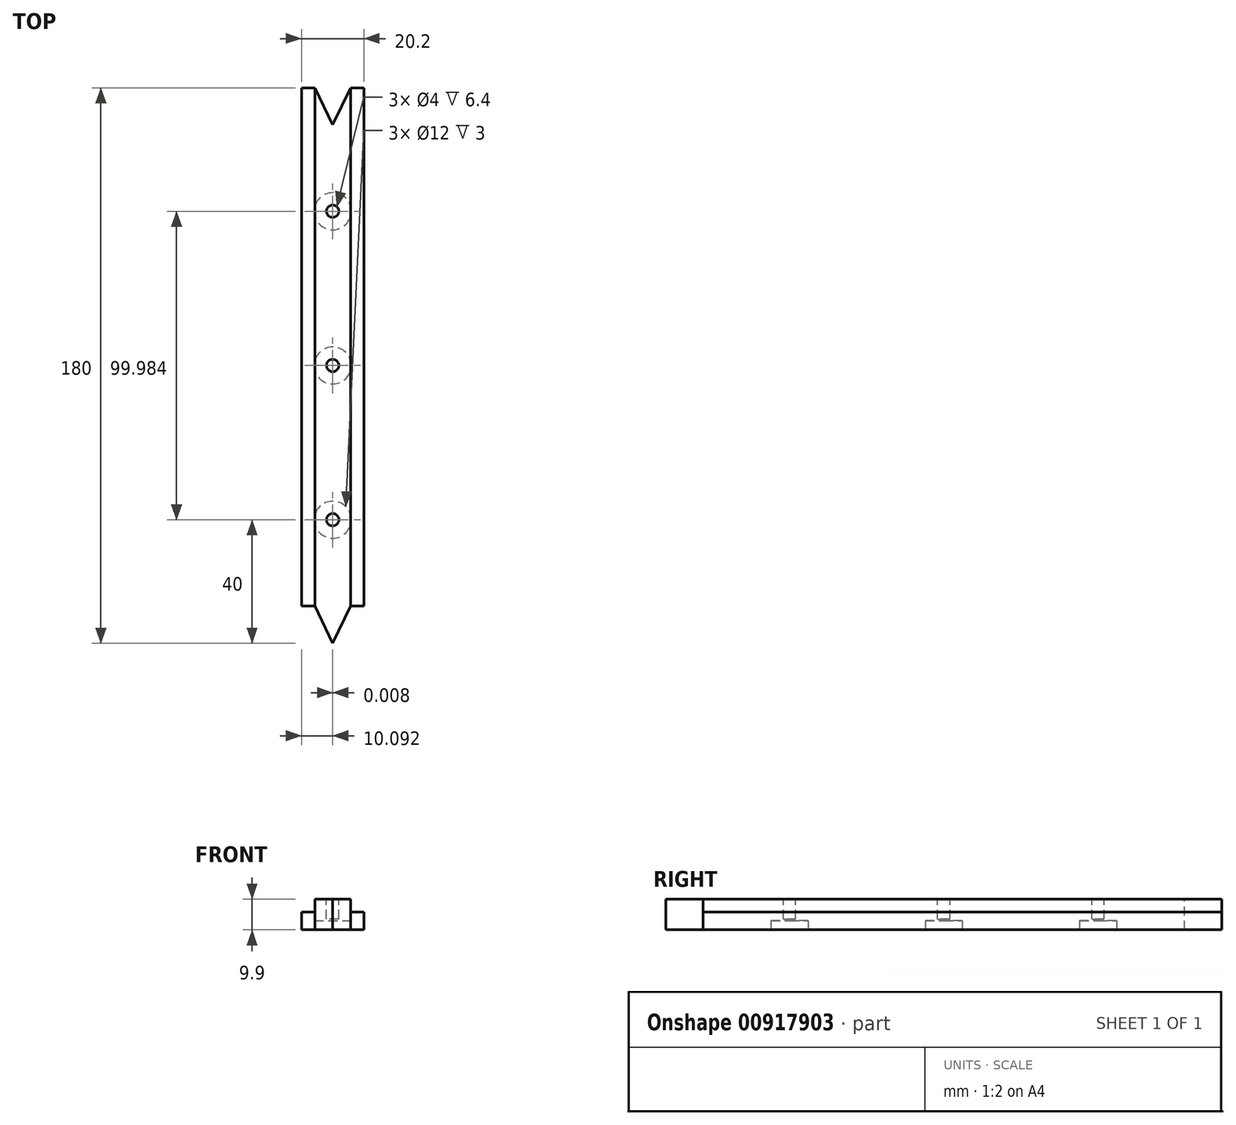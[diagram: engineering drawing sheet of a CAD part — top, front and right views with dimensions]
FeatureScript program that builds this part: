
annotation { "Feature Type Name" : "Feature", "Feature Type Description" : "" }
export const myFeature = defineFeature(function(context is Context, id is Id, definition is map)
    precondition{}
    {
        {
            var Q0;
            Q0=qCreatedBy(makeId("Front.planeOp"),FACE);
            var sketch = newSketch(context, id + "F0", { "sketchPlane" : qUnion([Q0])});
            skLineSegment(sketch, "E0.bottom", {"start": v(-10.1, 4.7) * mm, "end": v(10.1, 4.7) * mm});
            skLineSegment(sketch, "E0.top", {"start": v(-10.1, -4.7) * mm, "end": v(10.1, -4.7) * mm});
            skLineSegment(sketch, "E0.left", {"start": v(-10.1, 4.7) * mm, "end": v(-10.1, -4.7) * mm});
            skLineSegment(sketch, "E0.right", {"start": v(10.1, 4.7) * mm, "end": v(10.1, -4.7) * mm});
            skPoint(sketch, "E0.middle", {"position": v(0, 0) * mm});
            skLineSegment(sketch, "E1.bottom", {"start": v(-10.1, 4.7) * mm, "end": v(-5.8, 4.7) * mm});
            skLineSegment(sketch, "E1.top", {"start": v(-10.1, 0.5) * mm, "end": v(-5.8, 0.5) * mm});
            skLineSegment(sketch, "E1.left", {"start": v(-10.1, 4.7) * mm, "end": v(-10.1, 0.5) * mm});
            skLineSegment(sketch, "E1.right", {"start": v(-5.8, 4.7) * mm, "end": v(-5.8, 0.5) * mm});
            skLineSegment(sketch, "E2.bottom", {"start": v(10.1, 4.7) * mm, "end": v(5.8, 4.7) * mm});
            skLineSegment(sketch, "E2.top", {"start": v(10.1, 0.5) * mm, "end": v(5.8, 0.5) * mm});
            skLineSegment(sketch, "E2.left", {"start": v(10.1, 4.7) * mm, "end": v(10.1, 0.5) * mm});
            skLineSegment(sketch, "E2.right", {"start": v(5.8, 4.7) * mm, "end": v(5.8, 0.5) * mm});
            skSolve(sketch);
        }
        {
            var Q0;
            {var subQ1=sQuery(id+"F0.wireOp",EDGE,"E0.top");Q0=makeQuery(id+"F0.imprint","IMPRINT",FACE,{"disambiguationData":[TD([[makeQuery(id+"F0.imprint","IMPRINT",EDGE,{"derivedFrom":subQ1}),1.0]])]});}
            extrude(context, id + "F1", {"entities" : qUnion([Q0]), "depth" : 180 * mm, "offsetDistance" : 25 * mm});
        }
        {
            var Q0;
            Q0=makeQuery(id+"F1.opExtrude","SWEPT_FACE",FACE,{"disambiguationData":[OSD([sQuery(id+"F0.wireOp",EDGE,"E0.bottom")])]});
            var sketch = newSketch(context, id + "F2", { "sketchPlane" : qUnion([Q0])});
            skLineSegment(sketch, "E3", {"start": v(0, -180) * mm, "end": v(0, 0) * mm, "construction": true});
            skLineSegment(sketch, "E4.bottom", {"start": v(-5.8, -180) * mm, "end": v(5.8, -180) * mm, "construction": true});
            skLineSegment(sketch, "E4.top", {"start": v(-5.8, -140) * mm, "end": v(5.8, -140) * mm, "construction": true});
            skLineSegment(sketch, "E4.left", {"start": v(-5.8, -180) * mm, "end": v(-5.8, -140) * mm, "construction": true});
            skLineSegment(sketch, "E4.right", {"start": v(5.8, -180) * mm, "end": v(5.8, -140) * mm, "construction": true});
            skLineSegment(sketch, "E5.bottom", {"start": v(-5.8, 0) * mm, "end": v(5.8, 0) * mm, "construction": true});
            skLineSegment(sketch, "E5.top", {"start": v(-5.8, -40) * mm, "end": v(5.8, -40) * mm, "construction": true});
            skLineSegment(sketch, "E5.left", {"start": v(-5.8, 0) * mm, "end": v(-5.8, -40) * mm, "construction": true});
            skLineSegment(sketch, "E5.right", {"start": v(5.8, 0) * mm, "end": v(5.8, -40) * mm, "construction": true});
            skLineSegment(sketch, "E6.top", {"start": v(-5.8, -90) * mm, "end": v(5.8, -90) * mm, "construction": true});
            skLineSegment(sketch, "E6.left", {"start": v(-5.8, -140) * mm, "end": v(-5.8, -90) * mm, "construction": true});
            skLineSegment(sketch, "E6.right", {"start": v(5.8, -140) * mm, "end": v(5.8, -90) * mm, "construction": true});
            skCircle(sketch, "E7", {"center": v(0, -140) * mm, "radius": 2 * mm});
            skCircle(sketch, "E8", {"center": v(0, -90) * mm, "radius": 2 * mm});
            skCircle(sketch, "E9", {"center": v(0, -40.02) * mm, "radius": 2 * mm});
            skSolve(sketch);
        }
        {
            var Q0;
            Q0=makeQuery(id+"F2.imprint","IMPRINT",FACE,{"disambiguationData":[TD([[makeQuery(id+"F2.imprint","IMPRINT",EDGE,{"derivedFrom":sQuery(id+"F2.wireOp",EDGE,"E7")}),1.0]])]});
            var Q1;
            Q1=makeQuery(id+"F2.imprint","IMPRINT",FACE,{"disambiguationData":[TD([[makeQuery(id+"F2.imprint","IMPRINT",EDGE,{"derivedFrom":sQuery(id+"F2.wireOp",EDGE,"E8")}),1.0]])]});
            var Q2;
            Q2=makeQuery(id+"F2.imprint","IMPRINT",FACE,{"disambiguationData":[TD([[makeQuery(id+"F2.imprint","IMPRINT",EDGE,{"derivedFrom":sQuery(id+"F2.wireOp",EDGE,"E9")}),1.0]])]});
            extrude(context, id + "F3", {"entities" : qUnion([Q0, Q1, Q2]), "operationType" : NewBodyOperationType.REMOVE, "oppositeDirection" : true, "depth" : 25 * mm, "offsetDistance" : 25 * mm});
        }
        {
            var Q0;
            Q0=makeQuery(id+"F1.opExtrude","SWEPT_FACE",FACE,{"disambiguationData":[OSD([sQuery(id+"F0.wireOp",EDGE,"E0.top")])]});
            var sketch = newSketch(context, id + "F4", { "sketchPlane" : qUnion([Q0])});
            skLineSegment(sketch, "E10", {"start": v(0, 0) * mm, "end": v(0, 180) * mm, "construction": true});
            skLineSegment(sketch, "E11.bottom", {"start": v(-10.1, 0) * mm, "end": v(10.1, 0) * mm, "construction": true});
            skLineSegment(sketch, "E11.top", {"start": v(-10.1, 40) * mm, "end": v(10.1, 40) * mm, "construction": true});
            skLineSegment(sketch, "E11.left", {"start": v(-10.1, 0) * mm, "end": v(-10.1, 40) * mm, "construction": true});
            skLineSegment(sketch, "E11.right", {"start": v(10.1, 0) * mm, "end": v(10.1, 40) * mm, "construction": true});
            skLineSegment(sketch, "E12.top", {"start": v(-10.1, 90) * mm, "end": v(10.1, 90) * mm, "construction": true});
            skLineSegment(sketch, "E12.left", {"start": v(-10.1, 40) * mm, "end": v(-10.1, 90) * mm, "construction": true});
            skLineSegment(sketch, "E12.right", {"start": v(10.1, 40) * mm, "end": v(10.1, 90) * mm, "construction": true});
            skLineSegment(sketch, "E13.top", {"start": v(-10.1, 140) * mm, "end": v(10.1, 140) * mm, "construction": true});
            skLineSegment(sketch, "E13.left", {"start": v(-10.1, 90) * mm, "end": v(-10.1, 140) * mm, "construction": true});
            skLineSegment(sketch, "E13.right", {"start": v(10.1, 90) * mm, "end": v(10.1, 140) * mm, "construction": true});
            skCircle(sketch, "E14", {"center": v(0, 40.02) * mm, "radius": 6 * mm});
            skCircle(sketch, "E15", {"center": v(0, 90) * mm, "radius": 6 * mm});
            skCircle(sketch, "E16", {"center": v(0, 140) * mm, "radius": 6 * mm});
            skSolve(sketch);
        }
        {
            var Q0;
            Q0=makeQuery(id+"F4.imprint","IMPRINT",FACE,{"disambiguationData":[TD([[makeQuery(id+"F4.imprint","IMPRINT",EDGE,{"derivedFrom":sQuery(id+"F4.wireOp",EDGE,"E14")}),1.0]])]});
            var Q1;
            Q1=makeQuery(id+"F4.imprint","IMPRINT",FACE,{"disambiguationData":[TD([[makeQuery(id+"F4.imprint","IMPRINT",EDGE,{"derivedFrom":sQuery(id+"F4.wireOp",EDGE,"E15")}),1.0]])]});
            var Q2;
            Q2=makeQuery(id+"F4.imprint","IMPRINT",FACE,{"disambiguationData":[TD([[makeQuery(id+"F4.imprint","IMPRINT",EDGE,{"derivedFrom":sQuery(id+"F4.wireOp",EDGE,"E16")}),1.0]])]});
            extrude(context, id + "F5", {"entities" : qUnion([Q0, Q1, Q2]), "operationType" : NewBodyOperationType.REMOVE, "oppositeDirection" : true, "depth" : 3 * mm, "offsetDistance" : 25 * mm});
        }
        {
            var Q0;
            Q0=makeQuery(id+"F5.boolean.opBoolean","COPY",FACE,{"derivedFrom":makeQuery(id+"F5.opExtrude","CAP_FACE",FACE,{"disambiguationData":[OSD([sQuery(id+"F0.wireOp",EDGE,"E0.top"),sQuery(id+"F2.wireOp",EDGE,"E9"),sQuery(id+"F4.wireOp",EDGE,"E14")])],"isStart":false})});
            var sketch = newSketch(context, id + "F6", { "sketchPlane" : qUnion([Q0])});
            skLineSegment(sketch, "E17.bottom", {"start": v(-6.9, 31.88) * mm, "end": v(7.18, 31.88) * mm});
            skLineSegment(sketch, "E17.top", {"start": v(-6.9, 148.83) * mm, "end": v(7.18, 148.83) * mm});
            skLineSegment(sketch, "E17.left", {"start": v(-6.9, 31.88) * mm, "end": v(-6.9, 148.83) * mm});
            skLineSegment(sketch, "E17.right", {"start": v(7.18, 31.88) * mm, "end": v(7.18, 148.83) * mm});
            skSolve(sketch);
        }
        {
            var Q0;
            Q0 = qSketchRegion(id + "F6", true);
            var Q1;
            Q1=makeQuery(id+"F1.opExtrude","SWEPT_FACE",FACE,{"disambiguationData":[OSD([sQuery(id+"F0.wireOp",EDGE,"E0.top")])]});
            extrude(context, id + "F7", {"entities" : qUnion([Q0, Q1]), "operationType" : NewBodyOperationType.ADD, "depth" : 0.5 * mm, "offsetDistance" : 25 * mm});
        }
        {
            var Q0;
            Q0=makeQuery(id+"F1.opExtrude","SWEPT_FACE",FACE,{"disambiguationData":[OSD([sQuery(id+"F0.wireOp",EDGE,"E0.bottom")])]});
            var sketch = newSketch(context, id + "F8", { "sketchPlane" : qUnion([Q0])});
            skLineSegment(sketch, "E18.bottom", {"start": v(5.8, 0) * mm, "end": v(-5.8, 0) * mm, "construction": true});
            skLineSegment(sketch, "E18.top", {"start": v(5.8, -12) * mm, "end": v(-5.8, -12) * mm, "construction": true});
            skLineSegment(sketch, "E18.left", {"start": v(5.8, 0) * mm, "end": v(5.8, -12) * mm, "construction": true});
            skLineSegment(sketch, "E18.right", {"start": v(-5.8, 0) * mm, "end": v(-5.8, -12) * mm, "construction": true});
            skLineSegment(sketch, "E19.bottom", {"start": v(5.8, -180) * mm, "end": v(-5.8, -180) * mm, "construction": true});
            skLineSegment(sketch, "E19.top", {"start": v(5.8, -168) * mm, "end": v(-5.8, -168) * mm, "construction": true});
            skLineSegment(sketch, "E19.left", {"start": v(5.8, -180) * mm, "end": v(5.8, -168) * mm, "construction": true});
            skLineSegment(sketch, "E19.right", {"start": v(-5.8, -180) * mm, "end": v(-5.8, -168) * mm, "construction": true});
            skLineSegment(sketch, "E20", {"start": v(0, 0) * mm, "end": v(0, -180) * mm, "construction": true});
            skLineSegment(sketch, "E21", {"start": v(5.8, 0) * mm, "end": v(0, -12) * mm});
            skLineSegment(sketch, "E22", {"start": v(0, -12) * mm, "end": v(-5.8, 0) * mm});
            skLineSegment(sketch, "E23", {"start": v(5.8, -168) * mm, "end": v(-5.8, -168) * mm});
            skLineSegment(sketch, "E24", {"start": v(0, -180) * mm, "end": v(-5.8, -168) * mm});
            skLineSegment(sketch, "E25", {"start": v(5.8, -168) * mm, "end": v(0, -180) * mm});
            skSolve(sketch);
        }
        {
            var Q0;
            {var subQ0=sQuery(id+"F8.wireOp",EDGE,"E25");Q0=makeQuery(id+"F8.imprint","IMPRINT",FACE,{"disambiguationData":[TD([[makeQuery(id+"F8.imprint","IMPRINT",EDGE,{"derivedFrom":subQ0}),1.0]])]});}
            var Q1;
            {var subQ0=sQuery(id+"F8.wireOp",EDGE,"E24");Q1=makeQuery(id+"F8.imprint","IMPRINT",FACE,{"disambiguationData":[TD([[makeQuery(id+"F8.imprint","IMPRINT",EDGE,{"derivedFrom":subQ0}),1.0]])]});}
            var Q2;
            Q2=makeQuery(id+"F8.imprint","IMPRINT",FACE,{"disambiguationData":[TD([[makeQuery(id+"F8.imprint","IMPRINT",EDGE,{"derivedFrom":sQuery(id+"F8.wireOp",EDGE,"E21")}),-1.0]])]});
            extrude(context, id + "F9", {"entities" : qUnion([Q0, Q1, Q2]), "operationType" : NewBodyOperationType.REMOVE, "oppositeDirection" : true, "depth" : 25 * mm, "offsetDistance" : 25 * mm});
        }
        {
            var Q0;
            Q0=makeQuery(id+"F1.opExtrude","SWEPT_FACE",FACE,{"disambiguationData":[OSD([sQuery(id+"F0.wireOp",EDGE,"E2.top")])]});
            var sketch = newSketch(context, id + "F10", { "sketchPlane" : qUnion([Q0])});
            skLineSegment(sketch, "E26", {"start": v(5.8, -168) * mm, "end": v(11.07, -168) * mm, "construction": true});
            skLineSegment(sketch, "E27", {"start": v(11.07, -168) * mm, "end": v(-13.74, -168) * mm, "construction": true});
            skLineSegment(sketch, "E28.bottom", {"start": v(10.1, -180) * mm, "end": v(5.8, -180) * mm});
            skLineSegment(sketch, "E28.top", {"start": v(10.1, -168) * mm, "end": v(5.8, -168) * mm});
            skLineSegment(sketch, "E28.left", {"start": v(10.1, -180) * mm, "end": v(10.1, -168) * mm});
            skLineSegment(sketch, "E28.right", {"start": v(5.8, -180) * mm, "end": v(5.8, -168) * mm});
            skSolve(sketch);
        }
        {
            var Q0;
            Q0=makeQuery(id+"F10.imprint","IMPRINT",FACE,{"disambiguationData":[TD([[makeQuery(id+"F10.imprint","IMPRINT",EDGE,{"derivedFrom":sQuery(id+"F10.wireOp",EDGE,"E28.bottom")}),-1.0]])]});
            extrude(context, id + "F11", {"entities" : qUnion([Q0]), "operationType" : NewBodyOperationType.REMOVE, "oppositeDirection" : true, "depth" : 25 * mm, "offsetDistance" : 25 * mm});
        }
        {
            var Q0;
            Q0=makeQuery(id+"F1.opExtrude","SWEPT_FACE",FACE,{"disambiguationData":[OSD([sQuery(id+"F0.wireOp",EDGE,"E1.top")])]});
            var sketch = newSketch(context, id + "F12", { "sketchPlane" : qUnion([Q0])});
            skLineSegment(sketch, "E29.bottom", {"start": v(-5.8, -168) * mm, "end": v(-10.1, -168) * mm});
            skLineSegment(sketch, "E29.top", {"start": v(-5.8, -180) * mm, "end": v(-10.1, -180) * mm});
            skLineSegment(sketch, "E29.left", {"start": v(-5.8, -168) * mm, "end": v(-5.8, -180) * mm});
            skLineSegment(sketch, "E29.right", {"start": v(-10.1, -168) * mm, "end": v(-10.1, -180) * mm});
            skSolve(sketch);
        }
        {
            var Q0;
            Q0=makeQuery(id+"F12.imprint","IMPRINT",FACE,{"disambiguationData":[TD([[makeQuery(id+"F12.imprint","IMPRINT",EDGE,{"derivedFrom":sQuery(id+"F12.wireOp",EDGE,"E29.bottom")}),1.0]])]});
            extrude(context, id + "F13", {"entities" : qUnion([Q0]), "operationType" : NewBodyOperationType.REMOVE, "oppositeDirection" : true, "depth" : 25 * mm, "offsetDistance" : 25 * mm});
        }
    });
